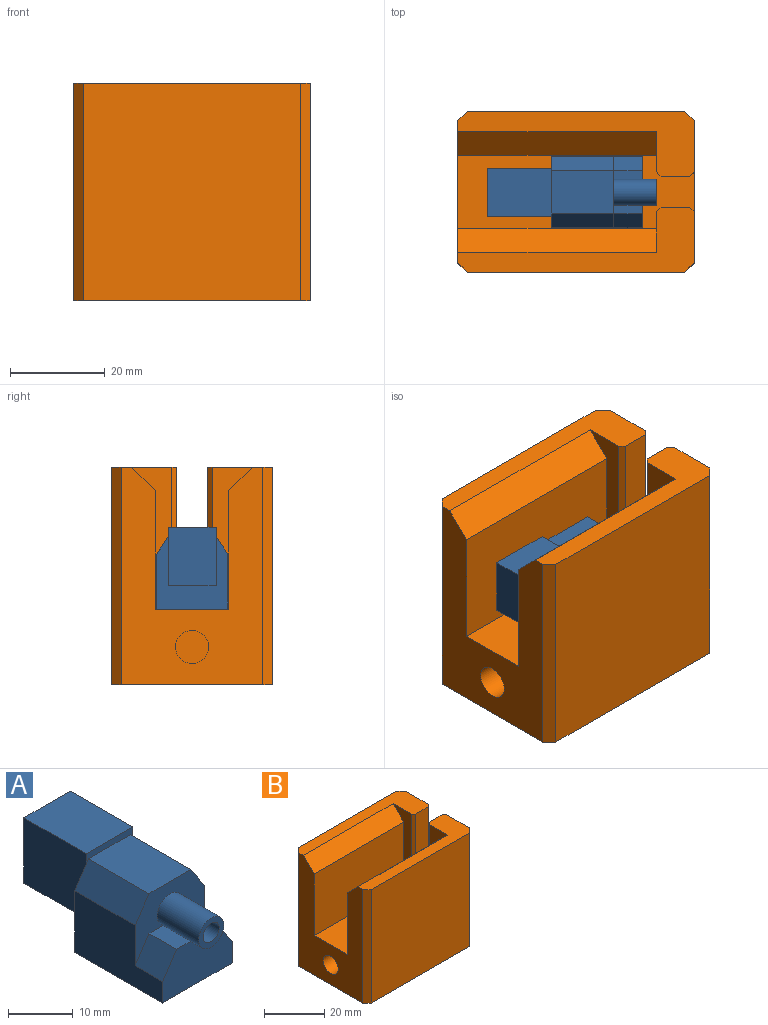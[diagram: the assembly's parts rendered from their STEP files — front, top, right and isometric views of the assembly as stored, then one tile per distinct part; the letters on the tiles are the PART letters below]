
ASSEMBLY  parts=2 mates=2
PART A: 23 faces, bbox 15.1x35.7x17.3 mm
  f0: plane 15.35x15.1mm, normal (0,1,0), area 117.9mm2, adj f1,f2,f3,f5,f6,f17,f18,f19
  f1: plane 19.15x11.6mm, normal (-1,0,0), area 176.5mm2, adj f0,f5,f6,f7,f14,f16
  f2: plane 19.15x11.6mm, normal (1,0,0), area 176.5mm2, adj f0,f3,f6,f7,f13,f16
  f3: plane 13.15x4.5mm, normal (0.83,0,0.55), area 71.1mm2, adj f0,f2,f4,f16,f22
  f4: plane 13.15x9.1mm, normal (0,0,1), area 119.7mm2, adj f3,f5,f16,f22
  f5: plane 13.15x4.5mm, normal (-0.83,0,0.55), area 71.1mm2, adj f0,f1,f4,f16,f22
  f6: plane 19.15x15.1mm, normal (0,0,-1), area 289.2mm2, adj f0,f1,f2,f7
  f7: plane 15.1x8.6mm, normal (0,-1,0), area 115.4mm2, adj f1,f2,f6,f9,f12,f13,f14,f15
  f8: cylinder r=1.75mm len=3.5mm, axis (0,1,0), area 33mm2, adj f10,f11
  f9: cylinder r=2.75mm len=9mm, axis (0,1,0), area 138.7mm2, adj f7,f10,f12,f15,f16
  f10: plane 5.5x5.5mm, normal (0,-1,0), area 14.1mm2, adj f8,f9
  f11: plane 3.5x3.5mm, normal (0,-1,0), area 9.6mm2, adj f8
  f12: plane 6x3.21mm, normal (0,0,1), area 19.2mm2, adj f7,f9,f13,f16
  f13: plane 6x4.6mm, normal (0.84,0,0.55), area 32.9mm2, adj f2,f7,f12,f16
  f14: plane 6x4.6mm, normal (-0.84,0,0.55), area 32.9mm2, adj f1,f7,f15,f16
  f15: plane 6x3.21mm, normal (0,0,1), area 19.2mm2, adj f7,f9,f14,f16
  f16: plane 15.1x12.1mm, normal (0,-1,0), area 90.4mm2, adj f1,f2,f3,f4,f5,f9,f12,f13
  f17: plane 13.55x12.3mm, normal (1,0,0), area 166.7mm2, adj f0,f18,f20,f21,f22
  f18: plane 13.55x10.1mm, normal (0,0,-1), area 136.9mm2, adj f0,f17,f19,f21
  f19: plane 13.55x12.3mm, normal (-1,0,0), area 166.7mm2, adj f0,f18,f20,f21,f22
  f20: plane 13.55x10.1mm, normal (0,0,1), area 136.9mm2, adj f17,f19,f21,f22
  f21: plane 12.3x10.1mm, normal (0,1,0), area 124.2mm2, adj f17,f18,f19,f20
  f22: plane 10.1x1.95mm, normal (0,-1,0), area 12.5mm2, adj f3,f4,f5,f17,f19,f20
PART B: 26 faces, bbox 50x34x46 mm
  f0: plane 30x8.5mm, normal (-1,0,0), area 117.5mm2, adj f1,f6,f14,f17,f24
  f1: plane 50x15.5mm, normal (0,0,1), area 705mm2, adj f0,f3,f4,f7,f10,f11,f14,f15
  f2: plane 50x13.75mm, normal (0,0,1), area 283.5mm2, adj f3,f4,f7,f9,f10,f16,f18,f20
  f3: plane 46x30mm, normal (1,0,0), area 1125mm2, adj f1,f2,f5,f6,f20,f21,f22,f23
  f4: plane 46x30mm, normal (-1,0,0), area 851.5mm2, adj f1,f2,f5,f6,f12,f14,f15,f16
  f5: plane 50x34mm, normal (0,0,-1), area 1692mm2, adj f3,f4,f8,f9,f18,f19,f20,f21
  f6: plane 50x13.75mm, normal (0,0,1), area 283.5mm2, adj f0,f3,f4,f8,f11,f17,f19,f21
  f7: plane 30x8.5mm, normal (-1,0,0), area 117.5mm2, adj f1,f2,f15,f16,f25
  f8: plane 46x46mm, normal (0,-1,0), area 2116mm2, adj f5,f6,f19,f21
  f9: plane 46x46mm, normal (0,1,0), area 2116mm2, adj f2,f5,f18,f20
  f10: plane 30x6mm, normal (0,-1,0), area 180mm2, adj f1,f2,f23,f25
  f11: plane 30x6mm, normal (0,1,0), area 180mm2, adj f1,f6,f22,f24
  f12: cylinder r=3.5mm len=7mm, axis (-1,0,0), area 131.9mm2, adj f4,f13
  f13: plane 7x7mm, normal (-1,0,0), area 38.5mm2, adj f12
  f14: plane 42x25mm, normal (0,1,0), area 1050mm2, adj f0,f1,f4,f17
  f15: plane 42x25mm, normal (0,-1,0), area 1050mm2, adj f1,f4,f7,f16
  f16: plane 42x5mm, normal (0,-0.71,0.71), area 297mm2, adj f2,f4,f7,f15
  f17: plane 42x5mm, normal (0,0.71,0.71), area 297mm2, adj f0,f4,f6,f14
  f18: plane 46x2mm, normal (-0.71,0.71,0), area 130.1mm2, adj f2,f4,f5,f9
  f19: plane 46x2mm, normal (-0.71,-0.71,0), area 130.1mm2, adj f4,f5,f6,f8
  f20: plane 46x2mm, normal (0.71,0.71,0), area 130.1mm2, adj f2,f3,f5,f9
  f21: plane 46x2mm, normal (0.71,-0.71,0), area 130.1mm2, adj f3,f5,f6,f8
  f22: plane 30x1mm, normal (0.71,0.71,0), area 42.4mm2, adj f1,f3,f6,f11
  f23: plane 30x1mm, normal (0.71,-0.71,0), area 42.4mm2, adj f1,f2,f3,f10
  f24: plane 30x1mm, normal (-0.71,0.71,0), area 42.4mm2, adj f0,f1,f6,f11
  f25: plane 30x1mm, normal (-0.71,-0.71,0), area 42.4mm2, adj f1,f2,f7,f10
PLACE A rot(axis=(0,0,1),90deg) t=(-5.15,-17.05,16.05)mm
PLACE B at identity fixed
MATE parallel B.f1 <-> A.f6  axis (0,0,1) through (-25,-17,8)mm
MATE parallel A.f8 <-> B.f0  axis (1,0,0) through (17,-17.05,19)mm
